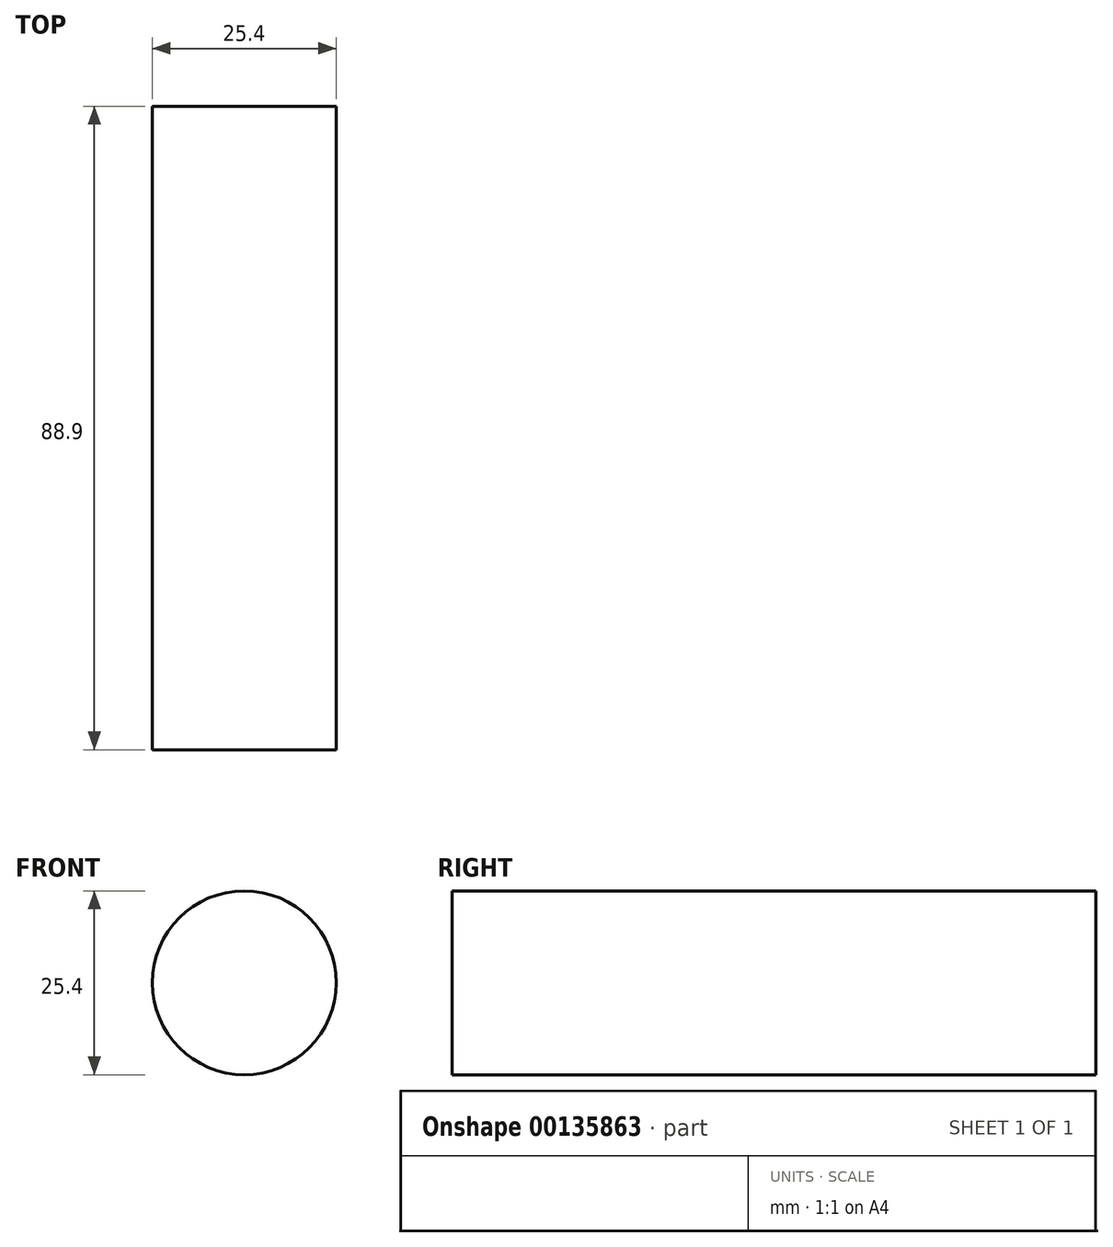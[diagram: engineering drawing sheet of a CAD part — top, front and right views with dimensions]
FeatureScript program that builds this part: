
annotation { "Feature Type Name" : "Feature", "Feature Type Description" : "" }
export const myFeature = defineFeature(function(context is Context, id is Id, definition is map)
    precondition{}
    {
        {
            var Q0;
            Q0=qCreatedBy(makeId("Front.planeOp"),FACE);
            cPlane(context, id + "F0", {"entities" : qUnion([Q0]), "cplaneType" : CPlaneType.OFFSET, "offset" : 12.7 * mm, "oppositeDirection" : true, "width" : 152.4 * mm, "height" : 152.4 * mm});
        }
        {
            var Q0;
            Q0=qCreatedBy(id+"F0.planeOp",FACE);
            var sketch = newSketch(context, id + "F1", { "sketchPlane" : qUnion([Q0])});
            skCircle(sketch, "E0", {"center": v(0, 0) * mm, "radius": 12.7 * mm});
            skSolve(sketch);
        }
        {
            var Q0;
            Q0=makeQuery(id+"F1.imprint","IMPRINT",FACE,{"disambiguationData":[TD([[makeQuery(id+"F1.imprint","IMPRINT",EDGE,{"derivedFrom":sQuery(id+"F1.wireOp",EDGE,"E0")}),1.0]])]});
            extrude(context, id + "F2", {"entities" : qUnion([Q0]), "depth" : 88.9 * mm});
        }
        {
            var Q0;
            Q0=makeQuery(id+"F2.opExtrude","CAP_FACE",FACE,{"disambiguationData":[OSD([sQuery(id+"F1.wireOp",EDGE,"E0")])],"isStart":false});
            cPlane(context, id + "F3", {"entities" : qUnion([Q0]), "cplaneType" : CPlaneType.OFFSET, "offset" : 12.7 * mm, "oppositeDirection" : true, "width" : 152.4 * mm, "height" : 152.4 * mm});
        }
    });
